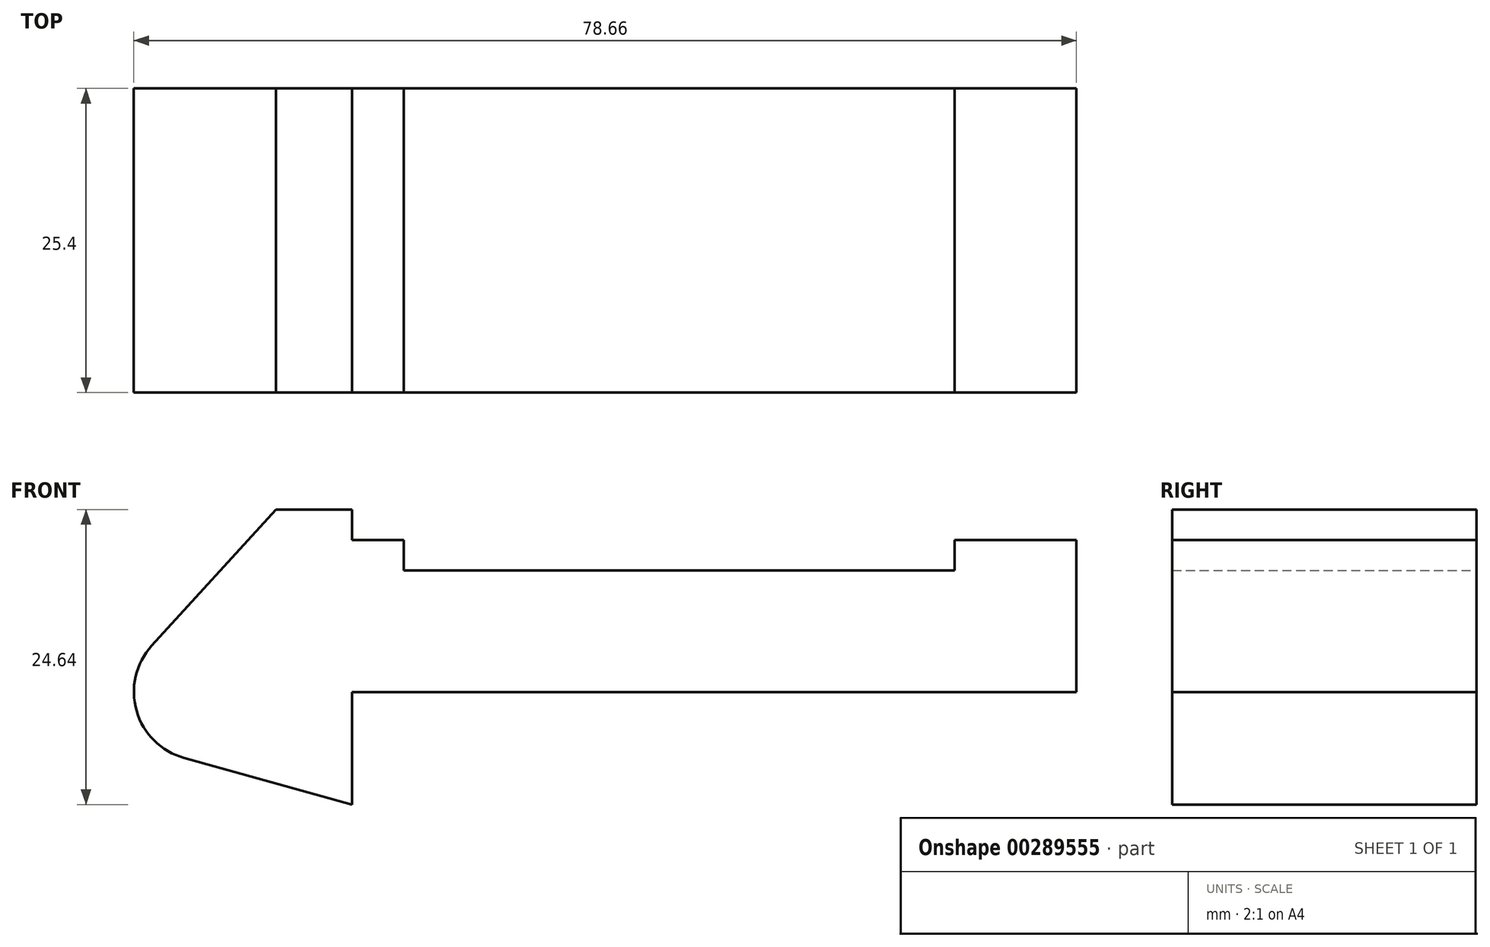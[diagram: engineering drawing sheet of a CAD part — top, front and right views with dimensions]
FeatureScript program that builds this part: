
annotation { "Feature Type Name" : "Feature", "Feature Type Description" : "" }
export const myFeature = defineFeature(function(context is Context, id is Id, definition is map)
    precondition{}
    {
        {
            var Q0;
            Q0=qCreatedBy(makeId("Front.planeOp"),FACE);
            var sketch = newSketch(context, id + "F0", { "sketchPlane" : qUnion([Q0])});
            skLineSegment(sketch, "E0", {"start": v(0, 0) * mm, "end": v(0, 12.7) * mm});
            skLineSegment(sketch, "E1", {"start": v(0, 12.7) * mm, "end": v(10.16, 12.7) * mm});
            skLineSegment(sketch, "E2", {"start": v(10.16, 12.7) * mm, "end": v(10.16, 10.16) * mm});
            skLineSegment(sketch, "E3", {"start": v(10.16, 10.16) * mm, "end": v(56.13, 10.16) * mm});
            skLineSegment(sketch, "E4", {"start": v(56.13, 10.16) * mm, "end": v(56.13, 12.7) * mm});
            skLineSegment(sketch, "E5", {"start": v(56.13, 12.7) * mm, "end": v(66.3, 12.7) * mm});
            skLineSegment(sketch, "E6", {"start": v(66.3, 12.7) * mm, "end": v(66.3, 0) * mm});
            skLineSegment(sketch, "E7", {"start": v(66.3, 0) * mm, "end": v(0, 0) * mm});
            skLineSegment(sketch, "E8", {"start": v(5.84, 15.24) * mm, "end": v(-0.5, 15.24) * mm});
            skLineSegment(sketch, "E9", {"start": v(-0.5, 15.24) * mm, "end": v(-10.88, 3.85) * mm});
            skLineSegment(sketch, "E10", {"start": v(0, 0) * mm, "end": v(-6.65, 0) * mm});
            skCircle(sketch, "E11", {"center": v(-6.65, 0) * mm, "radius": 5.72 * mm});
            skCircle(sketch, "E12", {"center": v(-6.65, 0) * mm, "radius": 3.18 * mm});
            skLineSegment(sketch, "E13", {"start": v(5.84, 15.24) * mm, "end": v(5.84, -9.4) * mm});
            skLineSegment(sketch, "E14", {"start": v(5.84, -9.4) * mm, "end": v(-8.18, -5.5) * mm});
            skSolve(sketch);
        }
        {
            var Q0;
            {var subQ0=sQuery(id+"F0.wireOp",EDGE,"E2");Q0=makeQuery(id+"F0.imprint","IMPRINT",FACE,{"disambiguationData":[TD([[makeQuery(id+"F0.imprint","IMPRINT",EDGE,{"derivedFrom":subQ0}),-1.0]])]});}
            var Q1;
            {var subQ1=sQuery(id+"F0.wireOp",EDGE,"E0");Q1=makeQuery(id+"F0.imprint","IMPRINT",FACE,{"disambiguationData":[TD([[makeQuery(id+"F0.imprint","IMPRINT",EDGE,{"derivedFrom":subQ1}),1.0]])]});}
            var Q2;
            {var subQ0=sQuery(id+"F0.wireOp",EDGE,"E0");Q2=makeQuery(id+"F0.imprint","IMPRINT",FACE,{"disambiguationData":[TD([[makeQuery(id+"F0.imprint","IMPRINT",EDGE,{"derivedFrom":subQ0}),-1.0]])]});}
            var Q3;
            {var subQ0=sQuery(id+"F0.wireOp",EDGE,"E14");Q3=makeQuery(id+"F0.imprint","IMPRINT",FACE,{"disambiguationData":[TD([[makeQuery(id+"F0.imprint","IMPRINT",EDGE,{"derivedFrom":subQ0}),-1.0]])]});}
            var Q4;
            {var subQ0=sQuery(id+"F0.wireOp",EDGE,"E12");Q4=makeQuery(id+"F0.imprint","IMPRINT",FACE,{"disambiguationData":[TD([[makeQuery(id+"F0.imprint","IMPRINT",EDGE,{"derivedFrom":subQ0}),1.0]])]});}
            var Q5;
            {var subQ5=sQuery(id+"F0.wireOp",EDGE,"E12");Q5=makeQuery(id+"F0.imprint","IMPRINT",FACE,{"disambiguationData":[TD([[makeQuery(id+"F0.imprint","IMPRINT",EDGE,{"derivedFrom":subQ5}),-1.0]])]});}
            extrude(context, id + "F1", {"entities" : qUnion([Q0, Q1, Q2, Q3, Q4, Q5]), "depth" : 25.4 * mm});
        }
    });
